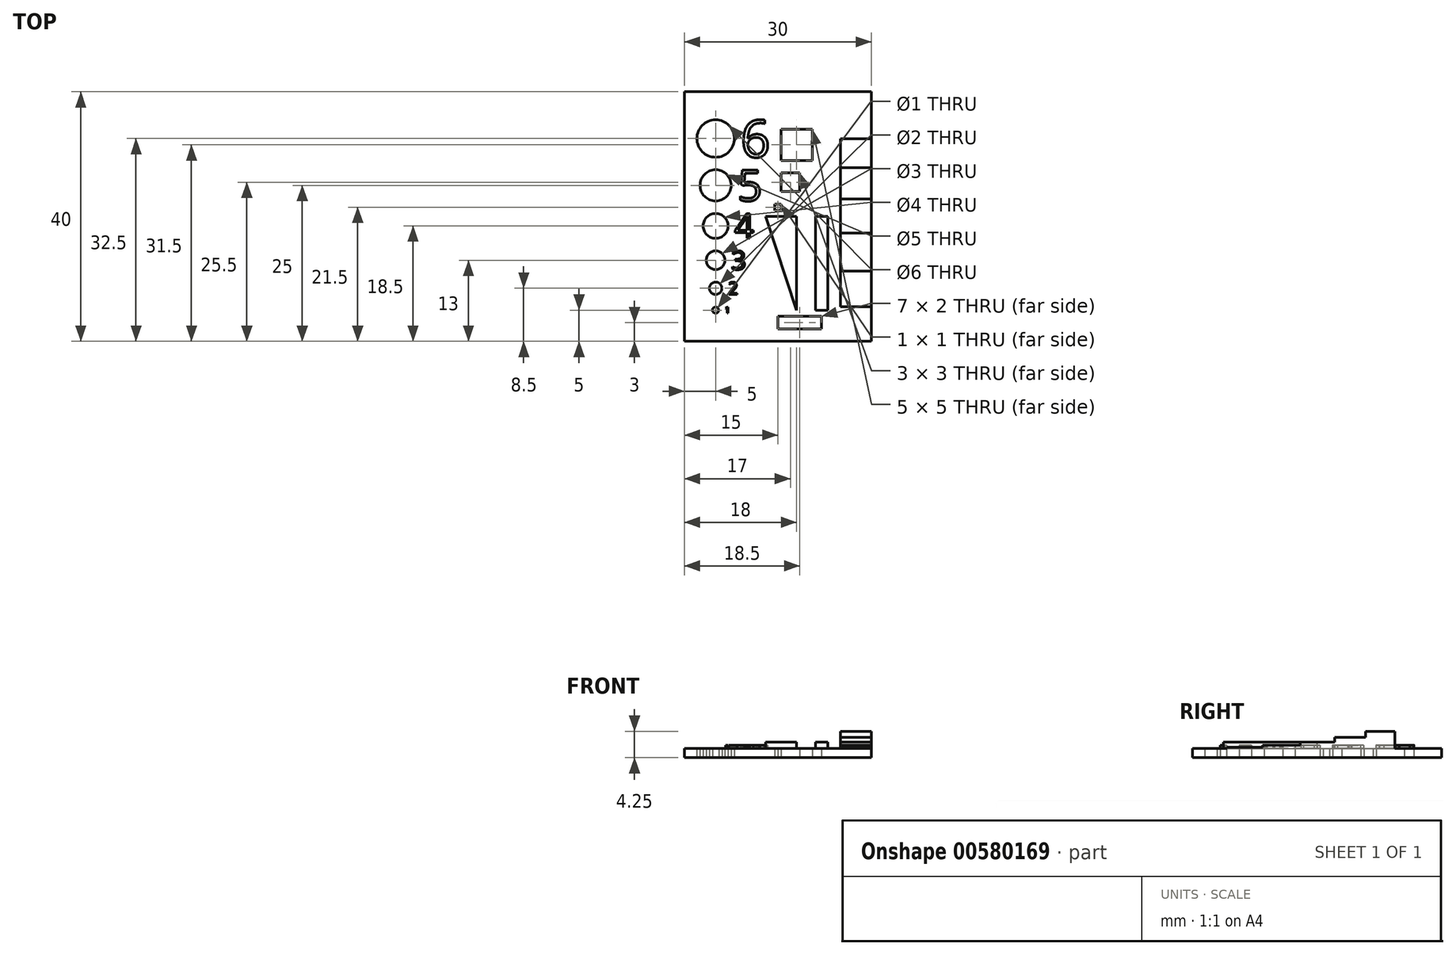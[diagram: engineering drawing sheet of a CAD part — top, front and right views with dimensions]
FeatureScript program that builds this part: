
annotation { "Feature Type Name" : "Feature", "Feature Type Description" : "" }
export const myFeature = defineFeature(function(context is Context, id is Id, definition is map)
    precondition{}
    {
        {
            var Q0;
            Q0=qCreatedBy(makeId("Top.planeOp"),FACE);
            var sketch = newSketch(context, id + "F0", { "sketchPlane" : qUnion([Q0])});
            skLineSegment(sketch, "E0.bottom", {"start": v(15, -20) * mm, "end": v(-15, -20) * mm});
            skLineSegment(sketch, "E0.top", {"start": v(15, 20) * mm, "end": v(-15, 20) * mm});
            skLineSegment(sketch, "E0.left", {"start": v(15, -20) * mm, "end": v(15, 20) * mm});
            skLineSegment(sketch, "E0.right", {"start": v(-15, -20) * mm, "end": v(-15, 20) * mm});
            skPoint(sketch, "E0.middle", {"position": v(0, 0) * mm});
            skLineSegment(sketch, "E1", {"start": v(-10, 17.65) * mm, "end": v(-10, -16.9) * mm, "construction": true});
            skCircle(sketch, "E2", {"center": v(-10, -15) * mm, "radius": 0.5 * mm});
            skCircle(sketch, "E3", {"center": v(-10, -11.5) * mm, "radius": 1 * mm});
            skCircle(sketch, "E4", {"center": v(-10, -7) * mm, "radius": 1.5 * mm});
            skCircle(sketch, "E5", {"center": v(-10, -1.5) * mm, "radius": 2 * mm});
            skCircle(sketch, "E6", {"center": v(-10, 5) * mm, "radius": 2.5 * mm});
            skLineSegment(sketch, "E7.bottom", {"start": v(5.5, 9) * mm, "end": v(0.5, 9) * mm});
            skLineSegment(sketch, "E7.top", {"start": v(5.5, 14) * mm, "end": v(0.5, 14) * mm});
            skLineSegment(sketch, "E7.left", {"start": v(5.5, 9) * mm, "end": v(5.5, 14) * mm});
            skLineSegment(sketch, "E7.right", {"start": v(0.5, 9) * mm, "end": v(0.5, 14) * mm});
            skPoint(sketch, "E7.middle", {"position": v(3, 11.5) * mm});
            skLineSegment(sketch, "E8.bottom", {"start": v(3.5, 4) * mm, "end": v(0.5, 4) * mm});
            skLineSegment(sketch, "E8.top", {"start": v(3.5, 7) * mm, "end": v(0.5, 7) * mm});
            skLineSegment(sketch, "E8.left", {"start": v(3.5, 4) * mm, "end": v(3.5, 7) * mm});
            skLineSegment(sketch, "E8.right", {"start": v(0.5, 4) * mm, "end": v(0.5, 7) * mm});
            skPoint(sketch, "E8.middle", {"position": v(2, 5.5) * mm});
            skLineSegment(sketch, "E9.bottom", {"start": v(0.5, 1) * mm, "end": v(-0.5, 1) * mm});
            skLineSegment(sketch, "E9.top", {"start": v(0.5, 2) * mm, "end": v(-0.5, 2) * mm});
            skLineSegment(sketch, "E9.left", {"start": v(0.5, 1) * mm, "end": v(0.5, 2) * mm});
            skLineSegment(sketch, "E9.right", {"start": v(-0.5, 1) * mm, "end": v(-0.5, 2) * mm});
            skPoint(sketch, "E9.middle", {"position": v(0, 1.5) * mm});
            skCircle(sketch, "E10", {"center": v(-10, 12.5) * mm, "radius": 3 * mm});
            skLineSegment(sketch, "E11.bottom", {"start": v(0, -18) * mm, "end": v(7, -18) * mm});
            skLineSegment(sketch, "E11.top", {"start": v(0, -16) * mm, "end": v(7, -16) * mm});
            skLineSegment(sketch, "E11.left", {"start": v(0, -18) * mm, "end": v(0, -16) * mm});
            skLineSegment(sketch, "E11.right", {"start": v(7, -18) * mm, "end": v(7, -16) * mm});
            skSolve(sketch);
        }
        {
            var Q0;
            Q0=makeQuery(id+"F0.imprint","IMPRINT",FACE,{"disambiguationData":[TD([[makeQuery(id+"F0.imprint","IMPRINT",EDGE,{"derivedFrom":sQuery(id+"F0.wireOp",EDGE,"E0.bottom")}),-1.0]])]});
            extrude(context, id + "F1", {"entities" : qUnion([Q0]), "depth" : 1.5 * mm, "offsetDistance" : 25 * mm});
        }
        {
            var Q0;
            Q0=makeQuery(id+"F1.opExtrude","SWEPT_FACE",FACE,{"disambiguationData":[OSD([sQuery(id+"F0.wireOp",EDGE,"E0.left")])]});
            var sketch = newSketch(context, id + "F2", { "sketchPlane" : qUnion([Q0])});
            skLineSegment(sketch, "E12", {"start": v(-14.44, 1.5) * mm, "end": v(-14.44, 1.7) * mm});
            skLineSegment(sketch, "E13", {"start": v(-14.44, 1.7) * mm, "end": v(-8.75, 1.7) * mm});
            skLineSegment(sketch, "E14", {"start": v(-8.75, 1.7) * mm, "end": v(-8.75, 2) * mm});
            skLineSegment(sketch, "E15", {"start": v(-8.75, 2) * mm, "end": v(-2.67, 2) * mm});
            skLineSegment(sketch, "E16", {"start": v(-2.67, 2) * mm, "end": v(-2.67, 2.5) * mm});
            skLineSegment(sketch, "E17", {"start": v(-2.67, 2.5) * mm, "end": v(2.8, 2.5) * mm});
            skLineSegment(sketch, "E18", {"start": v(2.8, 2.5) * mm, "end": v(2.8, 3.25) * mm});
            skLineSegment(sketch, "E19", {"start": v(2.8, 3.25) * mm, "end": v(7.8, 3.25) * mm});
            skLineSegment(sketch, "E20", {"start": v(7.8, 3.25) * mm, "end": v(7.8, 4.25) * mm});
            skLineSegment(sketch, "E21", {"start": v(7.8, 4.25) * mm, "end": v(12.5, 4.25) * mm});
            skLineSegment(sketch, "E22", {"start": v(12.5, 4.25) * mm, "end": v(12.5, 1.5) * mm});
            skLineSegment(sketch, "E23", {"start": v(12.5, 1.5) * mm, "end": v(-14.44, 1.5) * mm});
            skSolve(sketch);
        }
        {
            var Q0;
            Q0=makeQuery(id+"F2.imprint","IMPRINT",FACE,{"disambiguationData":[TD([[makeQuery(id+"F2.imprint","IMPRINT",EDGE,{"derivedFrom":sQuery(id+"F2.wireOp",EDGE,"E12")}),-1.0]])]});
            extrude(context, id + "F3", {"entities" : qUnion([Q0]), "operationType" : NewBodyOperationType.ADD, "oppositeDirection" : true, "depth" : 5 * mm, "offsetDistance" : 25 * mm});
        }
        {
            var Q0;
            Q0=makeQuery(id+"F1.opExtrude","CAP_FACE",FACE,{"disambiguationData":[OSD([sQuery(id+"F0.wireOp",EDGE,"E0.bottom"),sQuery(id+"F0.wireOp",EDGE,"E0.top"),sQuery(id+"F0.wireOp",EDGE,"E0.left"),sQuery(id+"F0.wireOp",EDGE,"E0.right"),sQuery(id+"F0.wireOp",EDGE,"E2"),sQuery(id+"F0.wireOp",EDGE,"E3"),sQuery(id+"F0.wireOp",EDGE,"E4"),sQuery(id+"F0.wireOp",EDGE,"E5"),sQuery(id+"F0.wireOp",EDGE,"E6"),sQuery(id+"F0.wireOp",EDGE,"E7.bottom"),sQuery(id+"F0.wireOp",EDGE,"E7.top"),sQuery(id+"F0.wireOp",EDGE,"E7.left"),sQuery(id+"F0.wireOp",EDGE,"E7.right"),sQuery(id+"F0.wireOp",EDGE,"E8.bottom"),sQuery(id+"F0.wireOp",EDGE,"E8.top"),sQuery(id+"F0.wireOp",EDGE,"E8.left"),sQuery(id+"F0.wireOp",EDGE,"E8.right"),sQuery(id+"F0.wireOp",EDGE,"E9.bottom"),sQuery(id+"F0.wireOp",EDGE,"E9.top"),sQuery(id+"F0.wireOp",EDGE,"E9.left"),sQuery(id+"F0.wireOp",EDGE,"E9.right"),sQuery(id+"F0.wireOp",EDGE,"E10")])],"isStart":false});
            var sketch = newSketch(context, id + "F4", { "sketchPlane" : qUnion([Q0])});
            skText(sketch, "E24", { "text": "6\n", "fontName": "OpenSans-Regular.ttf"});
            skText(sketch, "E25", { "text": "5", "fontName": "OpenSans-Regular.ttf"});
            skText(sketch, "E26", { "text": "4", "fontName": "OpenSans-Regular.ttf"});
            skText(sketch, "E27", { "text": "3", "fontName": "OpenSans-Regular.ttf"});
            skText(sketch, "E28", { "text": "2", "fontName": "OpenSans-Regular.ttf"});
            skText(sketch, "E29", { "text": "1", "fontName": "OpenSans-Regular.ttf"});
            const initialGuessF4  = {"E24": [-0.006, 0.0095, 1, 0, 0.006], "E25": [-0.0065, 0.0025, 1, 0, 0.005], "E26": [-0.007, -0.0035, 1, 0, 0.004], "E27": [-0.0075, -0.0085, 1, 0, 0.003], "E28": [-0.008, -0.0125, 1, 0, 0.002], "E29": [-0.0085, -0.0155, 1, 0, 0.001]};
            skSetInitialGuess(sketch, initialGuessF4);
            skSolve(sketch);
        }
        {
            var Q0;
            Q0 = qSketchRegion(id + "F4", true);
            extrude(context, id + "F5", {"entities" : qUnion([Q0]), "operationType" : NewBodyOperationType.ADD, "depth" : 0.5 * mm, "offsetDistance" : 25 * mm});
        }
        {
            var Q0;
            {var subQ0=sQuery(id+"F0.wireOp",EDGE,"E9.right");var subQ1=sQuery(id+"F0.wireOp",EDGE,"E9.left");var subQ2=sQuery(id+"F0.wireOp",EDGE,"E8.left");var subQ3=sQuery(id+"F0.wireOp",EDGE,"E8.top");var subQ4=sQuery(id+"F0.wireOp",EDGE,"E8.bottom");var subQ5=sQuery(id+"F0.wireOp",EDGE,"E7.right");var subQ6=sQuery(id+"F0.wireOp",EDGE,"E7.left");var subQ7=sQuery(id+"F0.wireOp",EDGE,"E7.top");var subQ8=sQuery(id+"F0.wireOp",EDGE,"E0.left");var subQ9=sQuery(id+"F0.wireOp",EDGE,"E0.top");var subQ10=sQuery(id+"F0.wireOp",EDGE,"E0.right");var subQ11=sQuery(id+"F0.wireOp",EDGE,"E10");var subQ12=sQuery(id+"F0.wireOp",EDGE,"E0.bottom");var subQ13=sQuery(id+"F0.wireOp",EDGE,"E7.bottom");var subQ14=sQuery(id+"F0.wireOp",EDGE,"E2");var subQ15=sQuery(id+"F0.wireOp",EDGE,"E3");var subQ16=sQuery(id+"F0.wireOp",EDGE,"E4");var subQ17=sQuery(id+"F0.wireOp",EDGE,"E5");var subQ18=sQuery(id+"F0.wireOp",EDGE,"E6");var subQ19=sQuery(id+"F0.wireOp",EDGE,"E8.right");var subQ21=sQuery(id+"F0.wireOp",EDGE,"E9.bottom");var subQ33=sQuery(id+"F0.wireOp",EDGE,"E9.top");Q0=makeQuery(id+"F5.boolean.opBoolean","SPLIT",FACE,{"disambiguationData":[TD([makeQuery(id+"F1.opExtrude","SWEPT_FACE",FACE,{"disambiguationData":[OSD([subQ12])]})])],"derivedFrom":makeQuery(id+"F1.opExtrude","CAP_FACE",FACE,{"disambiguationData":[OSD([subQ12,subQ9,subQ8,subQ10,subQ14,subQ15,subQ16,subQ17,subQ18,subQ13,subQ7,subQ6,subQ5,subQ4,subQ3,subQ2,subQ19,subQ21,subQ33,subQ1,subQ0,subQ11])],"isStart":false})});}
            var sketch = newSketch(context, id + "F6", { "sketchPlane" : qUnion([Q0])});
            skLineSegment(sketch, "E30", {"start": v(3, -15) * mm, "end": v(3, 0) * mm});
            skLineSegment(sketch, "E31", {"start": v(3, 0) * mm, "end": v(-2, 0) * mm});
            skLineSegment(sketch, "E32", {"start": v(-2, 0) * mm, "end": v(3, -15) * mm});
            skLineSegment(sketch, "E33.bottom", {"start": v(6, 0) * mm, "end": v(8, 0) * mm});
            skLineSegment(sketch, "E33.top", {"start": v(6, -15) * mm, "end": v(8, -15) * mm});
            skLineSegment(sketch, "E33.left", {"start": v(6, 0) * mm, "end": v(6, -15) * mm});
            skLineSegment(sketch, "E33.right", {"start": v(8, 0) * mm, "end": v(8, -15) * mm});
            skSolve(sketch);
        }
        {
            var Q0;
            Q0 = qSketchRegion(id + "F6", true);
            extrude(context, id + "F7", {"entities" : qUnion([Q0]), "operationType" : NewBodyOperationType.ADD, "depth" : 1 * mm, "offsetDistance" : 25 * mm});
        }
    });
